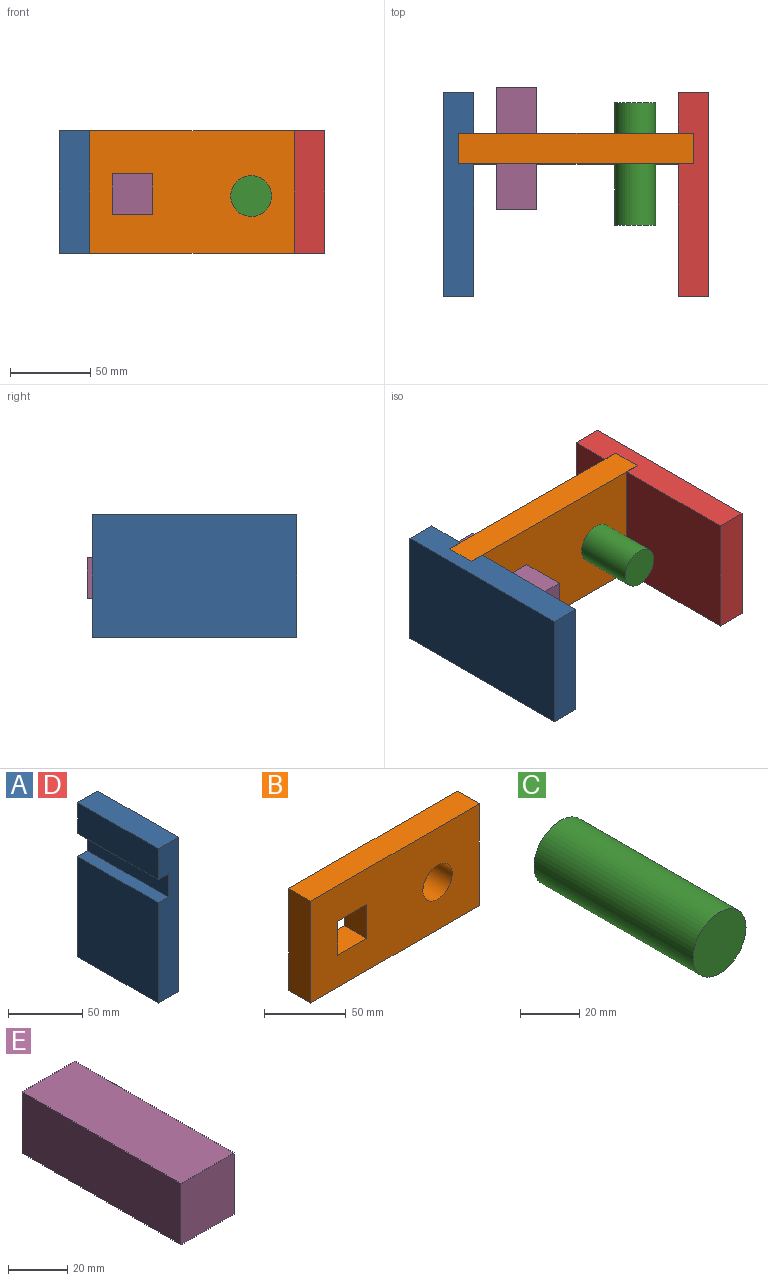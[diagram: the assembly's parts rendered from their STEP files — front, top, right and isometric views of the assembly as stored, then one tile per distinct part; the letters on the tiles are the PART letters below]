
ASSEMBLY  parts=5 mates=4
PART A: 10 faces, bbox 19.1x76.2x127 mm
  f0: plane 76.2x9.53mm, normal (0,0,1), area 725.8mm2, adj f1,f7,f8,f9
  f1: plane 82.55x76.2mm, normal (-1,0,0), area 6290.3mm2, adj f0,f2,f8,f9
  f2: plane 76.2x19.05mm, normal (0,0,-1), area 1451.6mm2, adj f1,f3,f8,f9
  f3: plane 127x76.2mm, normal (1,0,0), area 9677.4mm2, adj f2,f4,f8,f9
  f4: plane 76.2x19.05mm, normal (0,0,1), area 1451.6mm2, adj f3,f5,f8,f9
  f5: plane 76.2x25.4mm, normal (-1,0,0), area 1935.5mm2, adj f4,f6,f8,f9
  f6: plane 76.2x9.53mm, normal (0,0,-1), area 725.8mm2, adj f5,f7,f8,f9
  f7: plane 76.2x19.05mm, normal (-1,0,0), area 1451.6mm2, adj f0,f6,f8,f9
  f8: plane 127x19.05mm, normal (0,-1,0), area 2237.9mm2, adj f0,f1,f2,f3,f4,f5,f6,f7
  f9: plane 127x19.05mm, normal (0,1,0), area 2237.9mm2, adj f0,f1,f2,f3,f4,f5,f6,f7
PART B: 11 faces, bbox 146.1x19.1x76.2 mm
  f0: plane 146.05x19.05mm, normal (0,0,1), area 2782.3mm2, adj f1,f8,f9,f10
  f1: plane 76.2x19.05mm, normal (-1,0,0), area 1451.6mm2, adj f0,f2,f9,f10
  f2: plane 146.05x19.05mm, normal (0,0,-1), area 2782.3mm2, adj f1,f8,f9,f10
  f3: plane 25.4x19.05mm, normal (0,0,1), area 483.9mm2, adj f4,f6,f9,f10
  f4: plane 25.4x19.05mm, normal (1,0,0), area 483.9mm2, adj f3,f5,f9,f10
  f5: plane 25.4x19.05mm, normal (0,0,-1), area 483.9mm2, adj f4,f6,f9,f10
  f6: plane 25.4x19.05mm, normal (-1,0,0), area 483.9mm2, adj f3,f5,f9,f10
  f7: cylinder r=12.7mm len=25.4mm, axis (0,1,0), area 1520.1mm2, adj f9,f10
  f8: plane 76.2x19.05mm, normal (1,0,0), area 1451.6mm2, adj f0,f2,f9,f10
  f9: plane 146.05x76.2mm, normal (0,-1,0), area 9977.1mm2, adj f0,f1,f2,f3,f4,f5,f6,f7
  f10: plane 146.05x76.2mm, normal (0,1,0), area 9977.1mm2, adj f0,f1,f2,f3,f4,f5,f6,f7
PART C: 3 faces, bbox 25.4x76.2x25.4 mm
  f0: cylinder r=12.7mm len=76.2mm, axis (0,1,0), area 6080.5mm2, adj f1,f2
  f1: plane 25.4x25.4mm, normal (0,-1,0), area 506.7mm2, adj f0
  f2: plane 25.4x25.4mm, normal (0,1,0), area 506.7mm2, adj f0
PART D: same geometry as A
PART E: 6 faces, bbox 25.4x76.2x25.4 mm
  f0: plane 76.2x25.4mm, normal (-1,0,0), area 1935.5mm2, adj f1,f3,f4,f5
  f1: plane 76.2x25.4mm, normal (0,0,-1), area 1935.5mm2, adj f0,f2,f4,f5
  f2: plane 76.2x25.4mm, normal (1,0,0), area 1935.5mm2, adj f1,f3,f4,f5
  f3: plane 76.2x25.4mm, normal (0,0,1), area 1935.5mm2, adj f0,f2,f4,f5
  f4: plane 25.4x25.4mm, normal (0,-1,0), area 645.2mm2, adj f0,f1,f2,f3
  f5: plane 25.4x25.4mm, normal (0,1,0), area 645.2mm2, adj f0,f1,f2,f3
PLACE A rot(axis=(0,-0.71,-0.71),180deg) t=(67.35,-3.37,82.59)mm
PLACE B t=(130.96,41.71,39.23)mm fixed
PLACE C t=(203.54,60.76,23.05)mm
PLACE D rot(axis=(-1,0,0),90deg) t=(194.35,-3.37,6.39)mm
PLACE E t=(63.17,70.28,27.2)mm
MATE planar B.f1 <-> A.f7  axis (-1,0,0) through (57.82,32.18,44.49)mm
MATE planar E.f2 <-> B.f6  axis (1,0,0) through (106.52,32.18,43.15)mm
MATE planar C.f0 <-> B.f7  axis (0,1,0) through (167.65,22.66,41.96)mm
MATE planar B.f8 <-> D.f7  axis (1,0,0) through (203.87,32.18,44.49)mm
